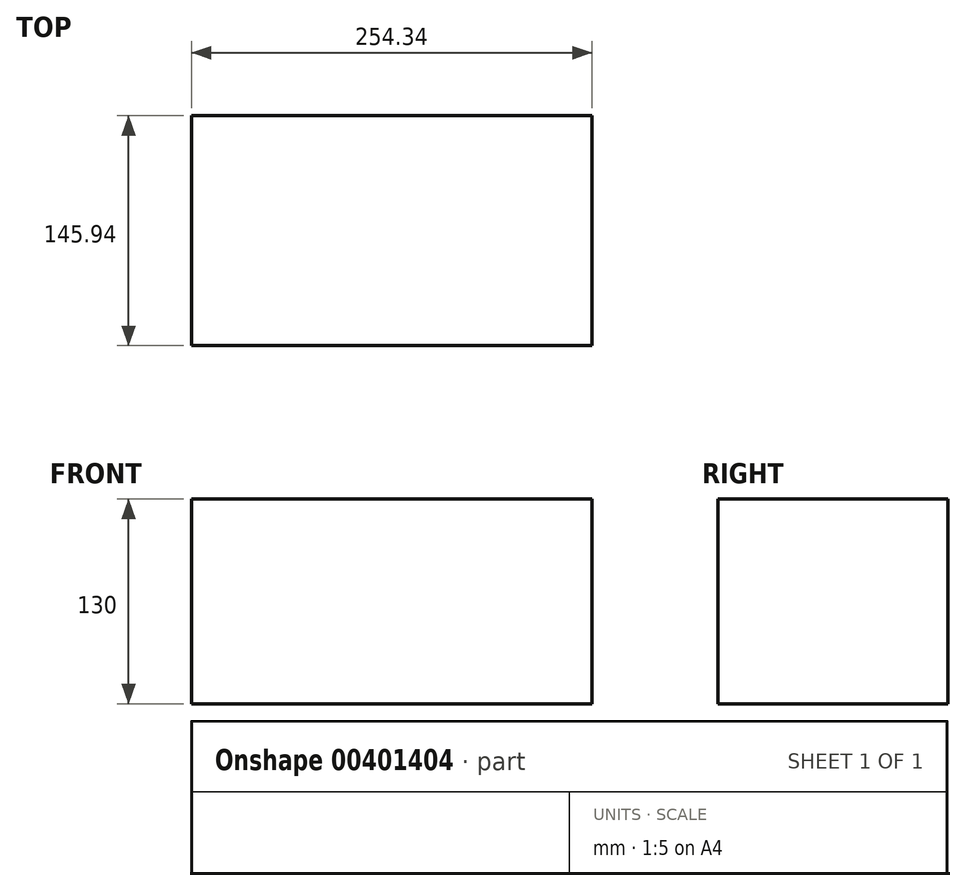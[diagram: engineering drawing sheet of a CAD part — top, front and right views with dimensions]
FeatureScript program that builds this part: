
annotation { "Feature Type Name" : "Feature", "Feature Type Description" : "" }
export const myFeature = defineFeature(function(context is Context, id is Id, definition is map)
    precondition{}
    {
        {
            var Q0;
            Q0=qCreatedBy(makeId("Top.planeOp"),FACE);
            var sketch = newSketch(context, id + "F0", { "sketchPlane" : qUnion([Q0])});
            skLineSegment(sketch, "E0.bottom", {"start": v(-122.5, -54.47) * mm, "end": v(131.84, -54.47) * mm});
            skLineSegment(sketch, "E0.top", {"start": v(-122.5, 91.47) * mm, "end": v(131.84, 91.47) * mm});
            skLineSegment(sketch, "E0.left", {"start": v(-122.5, -54.47) * mm, "end": v(-122.5, 91.47) * mm});
            skLineSegment(sketch, "E0.right", {"start": v(131.84, -54.47) * mm, "end": v(131.84, 91.47) * mm});
            skSolve(sketch);
        }
        {
            var Q0;
            Q0 = qSketchRegion(id + "F0", true);
            extrude(context, id + "F1", {"entities" : qUnion([Q0]), "depth" : 130 * mm});
        }
    });
